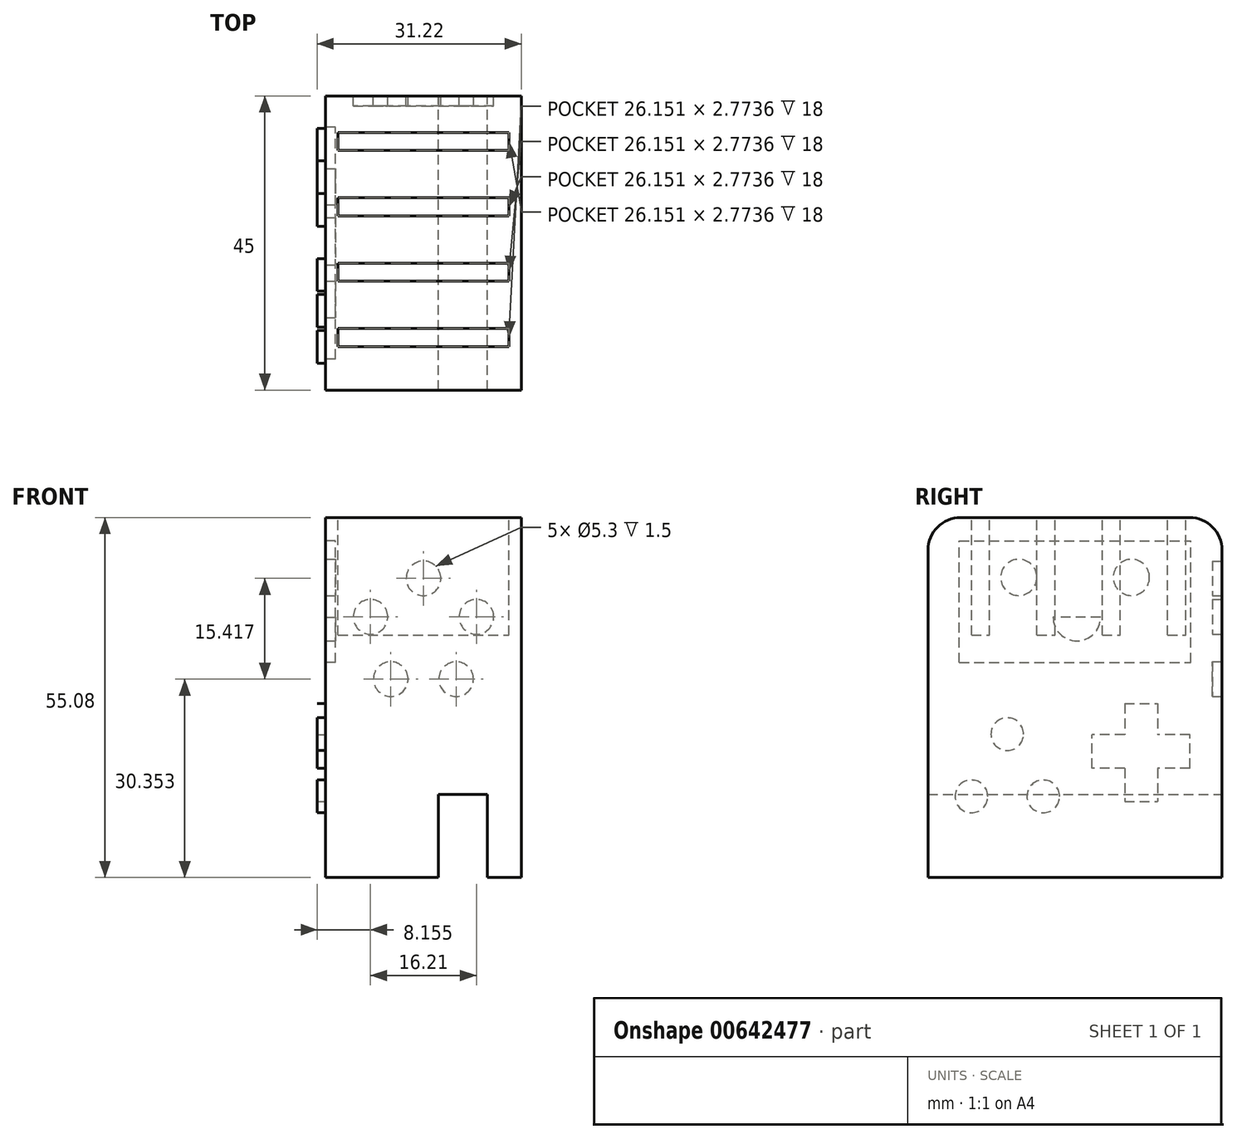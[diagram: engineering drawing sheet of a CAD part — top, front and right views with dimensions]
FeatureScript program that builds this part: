
annotation { "Feature Type Name" : "Feature", "Feature Type Description" : "" }
export const myFeature = defineFeature(function(context is Context, id is Id, definition is map)
    precondition{}
    {
        {
            var Q0;
            Q0=qCreatedBy(makeId("Front.planeOp"),FACE);
            var sketch = newSketch(context, id + "F0", { "sketchPlane" : qUnion([Q0])});
            skLineSegment(sketch, "E0.bottom", {"start": v(14.96, -27.54) * mm, "end": v(9.8, -27.54) * mm});
            skLineSegment(sketch, "E0.top", {"start": v(14.96, 27.54) * mm, "end": v(-14.96, 27.54) * mm});
            skLineSegment(sketch, "E0.left", {"start": v(14.96, -27.54) * mm, "end": v(14.96, 27.54) * mm});
            skLineSegment(sketch, "E0.right", {"start": v(-14.96, -27.54) * mm, "end": v(-14.96, 27.54) * mm});
            skPoint(sketch, "E0.middle", {"position": v(0, 0) * mm});
            skLineSegment(sketch, "E1.bottom", {"start": v(2.28, -14.86) * mm, "end": v(9.8, -14.86) * mm});
            skLineSegment(sketch, "E1.left", {"start": v(2.28, -14.86) * mm, "end": v(2.28, -27.54) * mm});
            skLineSegment(sketch, "E1.right", {"start": v(9.8, -14.86) * mm, "end": v(9.8, -27.54) * mm});
            skLineSegment(sketch, "E2.trimOffspring", {"start": v(2.28, -27.54) * mm, "end": v(-14.96, -27.54) * mm});
            skSolve(sketch);
        }
        {
            var Q0;
            Q0 = qSketchRegion(id + "F0", true);
            extrude(context, id + "F1", {"entities" : qUnion([Q0]), "endBound" : BoundingType.SYMMETRIC, "depth" : 45 * mm, "offsetDistance" : 25 * mm});
        }
        {
            var Q0;
            Q0=makeQuery(id+"F1.opExtrude","SWEPT_FACE",FACE,{"disambiguationData":[OSD([sQuery(id+"F0.wireOp",EDGE,"E0.top")])]});
            cPlane(context, id + "F2", {"entities" : qUnion([Q0]), "cplaneType" : CPlaneType.OFFSET, "offset" : 0 * mm, "width" : 150 * mm, "height" : 150 * mm});
        }
        {
            var Q0;
            Q0=qCreatedBy(id+"F2.planeOp",FACE);
            var sketch = newSketch(context, id + "F3", { "sketchPlane" : qUnion([Q0])});
            skLineSegment(sketch, "E3.bottom", {"start": v(-13.08, 14.17) * mm, "end": v(13.08, 14.17) * mm});
            skLineSegment(sketch, "E3.top", {"start": v(-13.08, 16.94) * mm, "end": v(13.08, 16.94) * mm});
            skLineSegment(sketch, "E3.left", {"start": v(-13.08, 14.17) * mm, "end": v(-13.08, 16.94) * mm});
            skLineSegment(sketch, "E3.right", {"start": v(13.08, 14.17) * mm, "end": v(13.08, 16.94) * mm});
            skPoint(sketch, "E3.middle", {"position": v(0, 15.55) * mm});
            skLineSegment(sketch, "E4.0.1.0", {"start": v(-13.08, 4.17) * mm, "end": v(13.08, 4.17) * mm});
            skLineSegment(sketch, "E4.0.2.0", {"start": v(-13.08, -5.83) * mm, "end": v(13.08, -5.83) * mm});
            skLineSegment(sketch, "E4.0.3.0", {"start": v(-13.08, -15.83) * mm, "end": v(13.08, -15.83) * mm});
            skLineSegment(sketch, "E4.direction1", {"start": v(-13.08, 14.17) * mm, "end": v(11.92, 14.17) * mm, "construction": true});
            skLineSegment(sketch, "E4.direction2", {"start": v(-13.08, 6.94) * mm, "end": v(-13.08, 4.17) * mm, "construction": true});
            skLineSegment(sketch, "E5.0.1.0", {"start": v(13.08, 4.17) * mm, "end": v(13.08, 6.94) * mm});
            skLineSegment(sketch, "E5.0.1.1", {"start": v(-13.08, 6.94) * mm, "end": v(13.08, 6.94) * mm});
            skLineSegment(sketch, "E5.0.1.2", {"start": v(-13.08, 4.17) * mm, "end": v(-13.08, 6.94) * mm});
            skLineSegment(sketch, "E5.0.2.0", {"start": v(13.08, -5.83) * mm, "end": v(13.08, -3.06) * mm});
            skLineSegment(sketch, "E5.0.2.1", {"start": v(-13.08, -3.06) * mm, "end": v(13.08, -3.06) * mm});
            skLineSegment(sketch, "E5.0.2.2", {"start": v(-13.08, -5.83) * mm, "end": v(-13.08, -3.06) * mm});
            skLineSegment(sketch, "E5.0.3.0", {"start": v(13.08, -15.83) * mm, "end": v(13.08, -13.06) * mm});
            skLineSegment(sketch, "E5.0.3.1", {"start": v(-13.08, -13.06) * mm, "end": v(13.08, -13.06) * mm});
            skLineSegment(sketch, "E5.0.3.2", {"start": v(-13.08, -15.83) * mm, "end": v(-13.08, -13.06) * mm});
            skLineSegment(sketch, "E5.direction2", {"start": v(13.08, 6.94) * mm, "end": v(13.08, 4.17) * mm, "construction": true});
            skSolve(sketch);
        }
        {
            var Q0;
            Q0 = qSketchRegion(id + "F3", true);
            extrude(context, id + "F4", {"entities" : qUnion([Q0]), "operationType" : NewBodyOperationType.REMOVE, "oppositeDirection" : true, "depth" : 18 * mm, "offsetDistance" : 25 * mm});
        }
        {
            var Q0;
            Q0=makeQuery(id+"F1.opExtrude","SWEPT_FACE",FACE,{"disambiguationData":[OSD([sQuery(id+"F0.wireOp",EDGE,"E0.right")])]});
            cPlane(context, id + "F5", {"entities" : qUnion([Q0]), "cplaneType" : CPlaneType.OFFSET, "offset" : 0 * mm, "width" : 150 * mm, "height" : 150 * mm});
        }
        {
            var Q0;
            Q0=qCreatedBy(id+"F5.planeOp",FACE);
            var sketch = newSketch(context, id + "F6", { "sketchPlane" : qUnion([Q0])});
            skLineSegment(sketch, "E6.bottom", {"start": v(17.73, 5.35) * mm, "end": v(-17.73, 5.35) * mm});
            skLineSegment(sketch, "E6.top", {"start": v(17.73, 23.97) * mm, "end": v(-17.73, 23.97) * mm});
            skLineSegment(sketch, "E6.left", {"start": v(17.73, 5.35) * mm, "end": v(17.73, 23.97) * mm});
            skLineSegment(sketch, "E6.right", {"start": v(-17.73, 5.35) * mm, "end": v(-17.73, 23.97) * mm});
            skPoint(sketch, "E6.middle", {"position": v(0, 14.66) * mm});
            skSolve(sketch);
        }
        {
            var Q0;
            Q0=makeQuery(id+"F1.opExtrude","CAP_EDGE",EDGE,{"disambiguationData":[OSD([sQuery(id+"F0.wireOp",EDGE,"E0.top")])],"isStart":false});
            var Q1;
            Q1=makeQuery(id+"F1.opExtrude","CAP_EDGE",EDGE,{"disambiguationData":[OSD([sQuery(id+"F0.wireOp",EDGE,"E0.top")])],"isStart":true});
            fillet(context, id + "F7", {"entities" : qUnion([Q0, Q1]), "radius" : 5 * mm, "tangentPropagation" : true, "allowEdgeOverflow" : false});
        }
        {
            var Q0;
            Q0 = qSketchRegion(id + "F6", true);
            extrude(context, id + "F8", {"entities" : qUnion([Q0]), "operationType" : NewBodyOperationType.REMOVE, "oppositeDirection" : true, "depth" : 1.5 * mm, "offsetDistance" : 25 * mm});
        }
        {
            var Q0;
            Q0=makeQuery(id+"F8.boolean.opBoolean","COPY",FACE,{"derivedFrom":makeQuery(id+"F8.opExtrude","CAP_FACE",FACE,{"disambiguationData":[OSD([sQuery(id+"F6.wireOp",EDGE,"E6.bottom"),sQuery(id+"F6.wireOp",EDGE,"E6.top"),sQuery(id+"F6.wireOp",EDGE,"E6.left"),sQuery(id+"F6.wireOp",EDGE,"E6.right")])],"isStart":false})});
            cPlane(context, id + "F9", {"entities" : qUnion([Q0]), "cplaneType" : CPlaneType.OFFSET, "offset" : 0 * mm, "width" : 150 * mm, "height" : 150 * mm});
        }
        {
            var Q0;
            Q0=qCreatedBy(id+"F9.planeOp",FACE);
            var sketch = newSketch(context, id + "F10", { "sketchPlane" : qUnion([Q0])});
            skCircle(sketch, "E7", {"center": v(-8.62, 18.38) * mm, "radius": 2.77 * mm});
            skCircle(sketch, "E8.MirrorC", {"center": v(8.62, 18.38) * mm, "radius": 2.77 * mm});
            skArc(sketch, "E9", {"start": v(-3.9, 12.3) * mm, "mid": v(-0.27, 8.67) * mm, "end": v(3.36, 12.3) * mm});
            skLineSegment(sketch, "E10", {"start": v(-3.9, 12.3) * mm, "end": v(3.36, 12.3) * mm});
            skSolve(sketch);
        }
        {
            var Q0;
            Q0 = qSketchRegion(id + "F10", true);
            extrude(context, id + "F11", {"entities" : qUnion([Q0]), "operationType" : NewBodyOperationType.ADD, "depth" : 1.5 * mm, "offsetDistance" : 25 * mm});
        }
        {
            var Q0;
            Q0=makeQuery(id+"F1.opExtrude","SWEPT_FACE",FACE,{"disambiguationData":[OSD([sQuery(id+"F0.wireOp",EDGE,"E0.right")])]});
            cPlane(context, id + "F12", {"entities" : qUnion([Q0]), "cplaneType" : CPlaneType.OFFSET, "offset" : 0 * mm, "width" : 150 * mm, "height" : 150 * mm});
        }
        {
            var Q0;
            Q0=qCreatedBy(id+"F12.planeOp",FACE);
            var sketch = newSketch(context, id + "F13", { "sketchPlane" : qUnion([Q0])});
            skLineSegment(sketch, "E11.bottom", {"start": v(-7.6, -15.94) * mm, "end": v(-12.61, -15.94) * mm});
            skLineSegment(sketch, "E11.left", {"start": v(-2.57, -10.83) * mm, "end": v(-2.57, -5.72) * mm});
            skPoint(sketch, "E11.middle", {"position": v(-10.07, -8.44) * mm});
            skLineSegment(sketch, "E12", {"start": v(-7.6, -0.94) * mm, "end": v(-12.61, -0.94) * mm});
            skLineSegment(sketch, "E13", {"start": v(-17.57, -10.83) * mm, "end": v(-17.57, -5.72) * mm});
            skLineSegment(sketch, "E14", {"start": v(-17.57, -5.72) * mm, "end": v(-12.61, -5.72) * mm});
            skPoint(sketch, "E14.endSnap0", {"position": v(-2.57, -8.44) * mm});
            skLineSegment(sketch, "E15", {"start": v(-17.57, -10.83) * mm, "end": v(-12.61, -10.83) * mm});
            skLineSegment(sketch, "E16", {"start": v(-12.61, -0.94) * mm, "end": v(-12.61, -5.72) * mm});
            skLineSegment(sketch, "E17", {"start": v(-7.6, -0.94) * mm, "end": v(-7.6, -5.72) * mm});
            skPoint(sketch, "E17.endSnap0", {"position": v(-10.07, -15.94) * mm});
            skPoint(sketch, "E18.end.orphan", {"position": v(-17.57, -0.94) * mm});
            skPoint(sketch, "E19.orphan", {"position": v(-2.57, -0.94) * mm});
            skLineSegment(sketch, "E20.trimOffspring", {"start": v(-7.6, -5.72) * mm, "end": v(-2.57, -5.72) * mm});
            skLineSegment(sketch, "E21.trimOffspring", {"start": v(-12.61, -10.83) * mm, "end": v(-12.61, -15.94) * mm});
            skLineSegment(sketch, "E22.trimOffspring", {"start": v(-7.6, -10.83) * mm, "end": v(-2.57, -10.83) * mm});
            skLineSegment(sketch, "E23.trimOffspring", {"start": v(-7.6, -10.83) * mm, "end": v(-7.6, -15.94) * mm});
            skPoint(sketch, "E24.orphan", {"position": v(-17.57, -15.94) * mm});
            skPoint(sketch, "E25.orphan", {"position": v(-2.57, -15.94) * mm});
            skSolve(sketch);
        }
        {
            var Q0;
            Q0=qCreatedBy(id+"F12.planeOp",FACE);
            var sketch = newSketch(context, id + "F14", { "sketchPlane" : qUnion([Q0])});
            skPoint(sketch, "E26.endSnap0", {"position": v(10.37, -15.14) * mm});
            skCircle(sketch, "E27", {"center": v(10.37, -5.6) * mm, "radius": 2.5 * mm});
            skCircle(sketch, "E28", {"center": v(4.87, -15.14) * mm, "radius": 2.5 * mm});
            skCircle(sketch, "E29", {"center": v(15.87, -15.14) * mm, "radius": 2.5 * mm});
            skSolve(sketch);
        }
        {
            var Q0;
            Q0 = qSketchRegion(id + "F13", true);
            var Q1;
            Q1 = qSketchRegion(id + "F14", true);
            extrude(context, id + "F15", {"entities" : qUnion([Q0, Q1]), "operationType" : NewBodyOperationType.ADD, "depth" : 1.3 * mm, "offsetDistance" : 25 * mm});
        }
        {
            var Q0;
            Q0=makeQuery(id+"F1.opExtrude","CAP_FACE",FACE,{"disambiguationData":[OSD([sQuery(id+"F0.wireOp",EDGE,"E0.bottom"),sQuery(id+"F0.wireOp",EDGE,"E0.top"),sQuery(id+"F0.wireOp",EDGE,"E0.left"),sQuery(id+"F0.wireOp",EDGE,"E0.right"),sQuery(id+"F0.wireOp",EDGE,"E1.bottom"),sQuery(id+"F0.wireOp",EDGE,"E1.left"),sQuery(id+"F0.wireOp",EDGE,"E1.right"),sQuery(id+"F0.wireOp",EDGE,"E2.trimOffspring")])],"isStart":true});
            cPlane(context, id + "F16", {"entities" : qUnion([Q0]), "cplaneType" : CPlaneType.OFFSET, "offset" : 0 * mm, "width" : 150 * mm, "height" : 150 * mm});
        }
        {
            var Q0;
            Q0=qCreatedBy(id+"F16.planeOp",FACE);
            var sketch = newSketch(context, id + "F17", { "sketchPlane" : qUnion([Q0])});
            skCircle(sketch, "E30", {"center": v(0, 18.23) * mm, "radius": 2.65 * mm});
            skCircle(sketch, "E31.1.0", {"center": v(8.1, 12.34) * mm, "radius": 2.65 * mm});
            skCircle(sketch, "E31.2.0", {"center": v(5, 2.81) * mm, "radius": 2.65 * mm});
            skCircle(sketch, "E31.3.0", {"center": v(-5, 2.81) * mm, "radius": 2.65 * mm});
            skCircle(sketch, "E31.4.0", {"center": v(-8.1, 12.34) * mm, "radius": 2.65 * mm});
            skPoint(sketch, "E31.center", {"position": v(0, 9.7) * mm});
            skLineSegment(sketch, "E31.anchor1", {"start": v(0, 9.7) * mm, "end": v(0, 18.23) * mm, "construction": true});
            skLineSegment(sketch, "E31.anchor2", {"start": v(0, 9.7) * mm, "end": v(-8.1, 12.34) * mm, "construction": true});
            skSolve(sketch);
        }
        {
            var Q0;
            Q0 = qSketchRegion(id + "F17", true);
            extrude(context, id + "F18", {"entities" : qUnion([Q0]), "operationType" : NewBodyOperationType.REMOVE, "oppositeDirection" : true, "depth" : 1.5 * mm, "offsetDistance" : 25 * mm});
        }
    });
